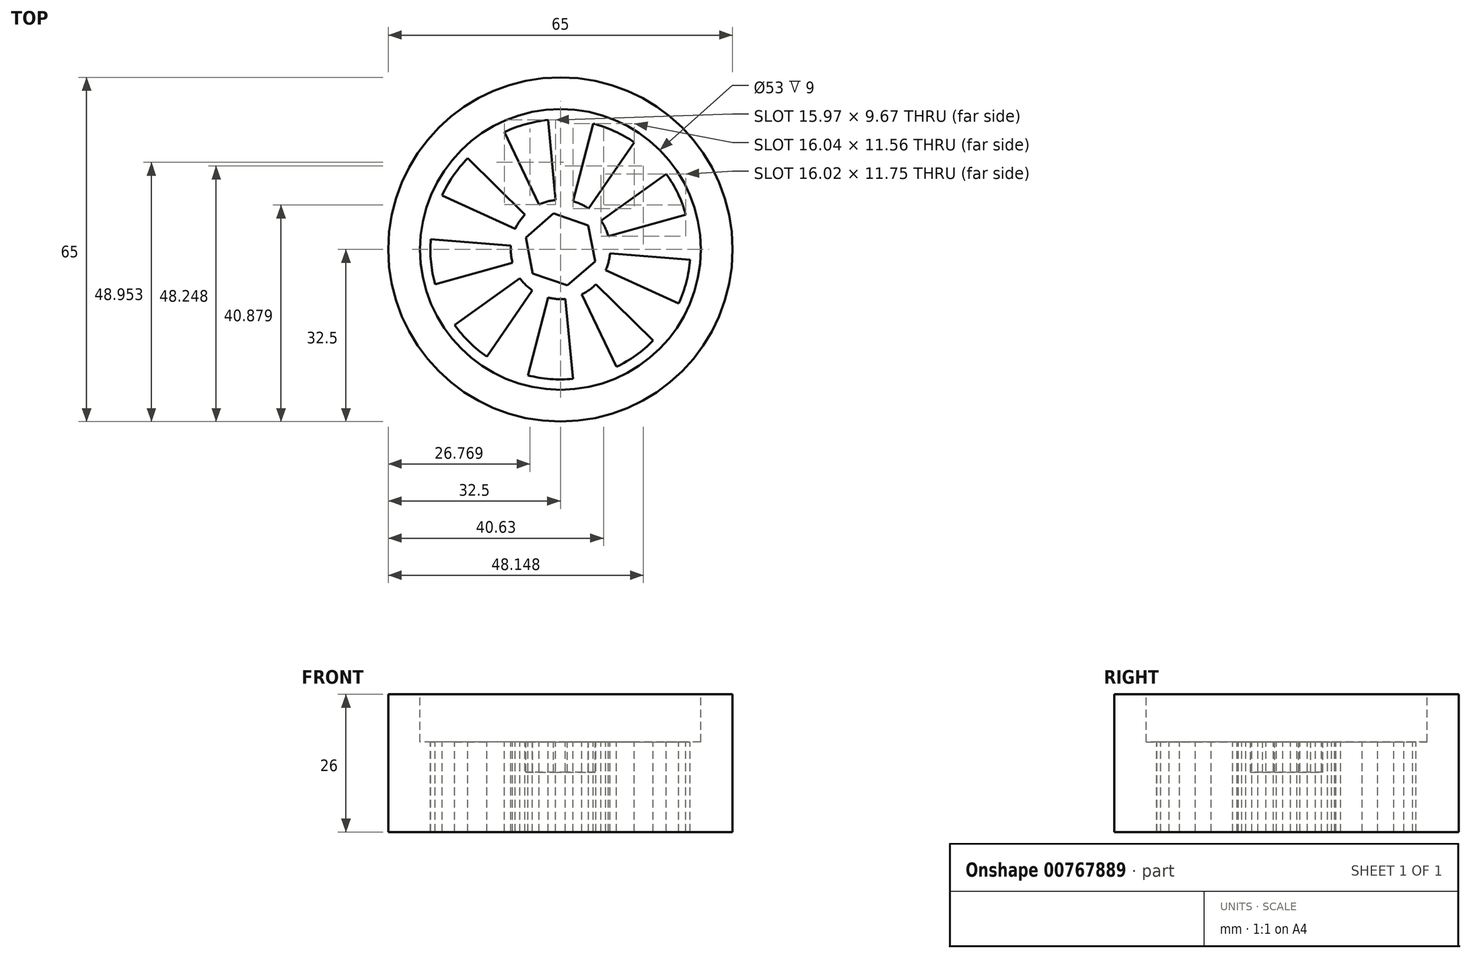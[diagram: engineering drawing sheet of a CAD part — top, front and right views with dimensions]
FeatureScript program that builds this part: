
annotation { "Feature Type Name" : "Feature", "Feature Type Description" : "" }
export const myFeature = defineFeature(function(context is Context, id is Id, definition is map)
    precondition{}
    {
        {
            var Q0;
            Q0=qCreatedBy(makeId("Top.planeOp"),FACE);
            var sketch = newSketch(context, id + "F0", { "sketchPlane" : qUnion([Q0])});
            skCircle(sketch, "E0", {"center": v(0, 0) * mm, "radius": 32.5 * mm});
            skSolve(sketch);
        }
        {
            var Q0;
            Q0=makeQuery(id+"F0.imprint","IMPRINT",FACE,{"disambiguationData":[TD([[makeQuery(id+"F0.imprint","IMPRINT",EDGE,{"derivedFrom":sQuery(id+"F0.wireOp",EDGE,"E0")}),1.0]])]});
            extrude(context, id + "F1", {"entities" : qUnion([Q0]), "depth" : 26 * mm, "offsetDistance" : 25 * mm});
        }
        {
            var Q0;
            Q0=makeQuery(id+"F1.opExtrude","CAP_FACE",FACE,{"disambiguationData":[OSD([sQuery(id+"F0.wireOp",EDGE,"E0")])],"isStart":false});
            var sketch = newSketch(context, id + "F2", { "sketchPlane" : qUnion([Q0])});
            skCircle(sketch, "E1.cCircle", {"center": v(0, 0) * mm, "radius": 6.93 * mm, "construction": true});
            skLineSegment(sketch, "E1.0", {"start": v(-5.24, -4.53) * mm, "end": v(-6.54, 2.27) * mm});
            skLineSegment(sketch, "E1.1", {"start": v(-6.54, 2.27) * mm, "end": v(-1.3, 6.8) * mm});
            skLineSegment(sketch, "E1.2", {"start": v(-1.3, 6.8) * mm, "end": v(5.24, 4.53) * mm});
            skLineSegment(sketch, "E1.3", {"start": v(5.24, 4.53) * mm, "end": v(6.54, -2.27) * mm});
            skLineSegment(sketch, "E1.4", {"start": v(6.54, -2.27) * mm, "end": v(1.3, -6.8) * mm});
            skLineSegment(sketch, "E1.5", {"start": v(1.3, -6.8) * mm, "end": v(-5.24, -4.53) * mm});
            skSolve(sketch);
        }
        {
            var Q0;
            Q0=makeQuery(id+"F2.imprint","IMPRINT",FACE,{"disambiguationData":[TD([[makeQuery(id+"F2.imprint","IMPRINT",EDGE,{"derivedFrom":sQuery(id+"F2.wireOp",EDGE,"E1.0")}),-1.0]])]});
            extrude(context, id + "F3", {"entities" : qUnion([Q0]), "operationType" : NewBodyOperationType.REMOVE, "oppositeDirection" : true, "depth" : 14.7 * mm, "offsetDistance" : 25 * mm});
        }
        {
            var Q0;
            Q0=makeQuery(id+"F1.opExtrude","CAP_FACE",FACE,{"disambiguationData":[OSD([sQuery(id+"F0.wireOp",EDGE,"E0")])],"isStart":false});
            var sketch = newSketch(context, id + "F4", { "sketchPlane" : qUnion([Q0])});
            skCircle(sketch, "E2", {"center": v(0, 0) * mm, "radius": 26.5 * mm});
            skSolve(sketch);
        }
        {
            var Q0;
            Q0=makeQuery(id+"F4.imprint","IMPRINT",FACE,{"disambiguationData":[TD([[makeQuery(id+"F4.imprint","IMPRINT",EDGE,{"derivedFrom":sQuery(id+"F4.wireOp",EDGE,"E2")}),1.0]])]});
            extrude(context, id + "F5", {"entities" : qUnion([Q0]), "operationType" : NewBodyOperationType.REMOVE, "oppositeDirection" : true, "depth" : 9 * mm, "offsetDistance" : 25 * mm});
        }
        {
            var Q0;
            Q0=makeQuery(id+"F5.boolean.opBoolean","COPY",FACE,{"derivedFrom":makeQuery(id+"F5.opExtrude","CAP_FACE",FACE,{"disambiguationData":[OSD([sQuery(id+"F2.wireOp",EDGE,"E1.0"),sQuery(id+"F2.wireOp",EDGE,"E1.1"),sQuery(id+"F2.wireOp",EDGE,"E1.2"),sQuery(id+"F2.wireOp",EDGE,"E1.3"),sQuery(id+"F2.wireOp",EDGE,"E1.4"),sQuery(id+"F2.wireOp",EDGE,"E1.5"),sQuery(id+"F4.wireOp",EDGE,"E2")])],"isStart":false})});
            var sketch = newSketch(context, id + "F6", { "sketchPlane" : qUnion([Q0])});
            skArc(sketch, "E3", {"start": v(-2.35, 24.44) * mm, "mid": v(-6.56, 23.66) * mm, "end": v(-10.56, 22.16) * mm});
            skLineSegment(sketch, "E4", {"start": v(-4.04, 8.47) * mm, "end": v(-10.56, 22.16) * mm});
            skLineSegment(sketch, "E5", {"start": v(-0.9, 9.34) * mm, "end": v(-2.35, 24.44) * mm});
            skArc(sketch, "E6", {"start": v(-0.9, 9.34) * mm, "mid": v(-2.5, 9.04) * mm, "end": v(-4.04, 8.47) * mm});
            skLineSegment(sketch, "E7.1.0", {"start": v(-8.53, 3.9) * mm, "end": v(-22.34, 10.19) * mm});
            skLineSegment(sketch, "E7.1.1", {"start": v(-6.69, 6.58) * mm, "end": v(-17.5, 17.21) * mm});
            skArc(sketch, "E7.1.2", {"start": v(-17.5, 17.21) * mm, "mid": v(-20.23, 13.91) * mm, "end": v(-22.34, 10.19) * mm});
            skArc(sketch, "E7.1.3", {"start": v(-6.69, 6.58) * mm, "mid": v(-7.73, 5.31) * mm, "end": v(-8.53, 3.9) * mm});
            skLineSegment(sketch, "E7.2.0", {"start": v(-9.04, -2.5) * mm, "end": v(-23.66, -6.56) * mm});
            skLineSegment(sketch, "E7.2.1", {"start": v(-9.35, 0.74) * mm, "end": v(-24.47, 1.93) * mm});
            skArc(sketch, "E7.2.2", {"start": v(-24.47, 1.93) * mm, "mid": v(-24.44, -2.35) * mm, "end": v(-23.66, -6.56) * mm});
            skArc(sketch, "E7.2.3", {"start": v(-9.35, 0.74) * mm, "mid": v(-9.34, -0.9) * mm, "end": v(-9.04, -2.5) * mm});
            skLineSegment(sketch, "E7.3.0", {"start": v(-5.31, -7.73) * mm, "end": v(-13.91, -20.23) * mm});
            skLineSegment(sketch, "E7.3.1", {"start": v(-7.64, -5.45) * mm, "end": v(-20, -14.25) * mm});
            skArc(sketch, "E7.3.2", {"start": v(-20, -14.25) * mm, "mid": v(-17.21, -17.5) * mm, "end": v(-13.91, -20.23) * mm});
            skArc(sketch, "E7.3.3", {"start": v(-7.64, -5.45) * mm, "mid": v(-6.58, -6.69) * mm, "end": v(-5.31, -7.73) * mm});
            skLineSegment(sketch, "E7.4.0", {"start": v(0.9, -9.34) * mm, "end": v(2.35, -24.44) * mm});
            skLineSegment(sketch, "E7.4.1", {"start": v(-2.35, -9.08) * mm, "end": v(-6.15, -23.77) * mm});
            skArc(sketch, "E7.4.2", {"start": v(-6.15, -23.77) * mm, "mid": v(-1.93, -24.47) * mm, "end": v(2.35, -24.44) * mm});
            skArc(sketch, "E7.4.3", {"start": v(-2.35, -9.08) * mm, "mid": v(-0.74, -9.35) * mm, "end": v(0.9, -9.34) * mm});
            skLineSegment(sketch, "E7.5.0", {"start": v(6.69, -6.58) * mm, "end": v(17.5, -17.21) * mm});
            skLineSegment(sketch, "E7.5.1", {"start": v(4.04, -8.47) * mm, "end": v(10.56, -22.16) * mm});
            skArc(sketch, "E7.5.2", {"start": v(10.56, -22.16) * mm, "mid": v(14.25, -20) * mm, "end": v(17.5, -17.21) * mm});
            skArc(sketch, "E7.5.3", {"start": v(4.04, -8.47) * mm, "mid": v(5.45, -7.64) * mm, "end": v(6.69, -6.58) * mm});
            skLineSegment(sketch, "E7.6.0", {"start": v(9.35, -0.74) * mm, "end": v(24.47, -1.93) * mm});
            skLineSegment(sketch, "E7.6.1", {"start": v(8.53, -3.9) * mm, "end": v(22.34, -10.19) * mm});
            skArc(sketch, "E7.6.2", {"start": v(22.34, -10.19) * mm, "mid": v(23.77, -6.15) * mm, "end": v(24.47, -1.93) * mm});
            skArc(sketch, "E7.6.3", {"start": v(8.53, -3.9) * mm, "mid": v(9.08, -2.35) * mm, "end": v(9.35, -0.74) * mm});
            skLineSegment(sketch, "E7.7.0", {"start": v(7.64, 5.45) * mm, "end": v(20, 14.25) * mm});
            skLineSegment(sketch, "E7.7.1", {"start": v(9.04, 2.5) * mm, "end": v(23.66, 6.56) * mm});
            skArc(sketch, "E7.7.2", {"start": v(23.66, 6.56) * mm, "mid": v(22.16, 10.56) * mm, "end": v(20, 14.25) * mm});
            skArc(sketch, "E7.7.3", {"start": v(9.04, 2.5) * mm, "mid": v(8.47, 4.04) * mm, "end": v(7.64, 5.45) * mm});
            skLineSegment(sketch, "E7.8.0", {"start": v(2.35, 9.08) * mm, "end": v(6.15, 23.77) * mm});
            skLineSegment(sketch, "E7.8.1", {"start": v(5.31, 7.73) * mm, "end": v(13.91, 20.23) * mm});
            skArc(sketch, "E7.8.2", {"start": v(13.91, 20.23) * mm, "mid": v(10.19, 22.34) * mm, "end": v(6.15, 23.77) * mm});
            skArc(sketch, "E7.8.3", {"start": v(5.31, 7.73) * mm, "mid": v(3.9, 8.53) * mm, "end": v(2.35, 9.08) * mm});
            skSolve(sketch);
        }
        {
            var Q0;
            Q0=makeQuery(id+"F6.imprint","IMPRINT",FACE,{"disambiguationData":[TD([[makeQuery(id+"F6.imprint","IMPRINT",EDGE,{"derivedFrom":sQuery(id+"F6.wireOp",EDGE,"E7.1.0")}),-1.0]])]});
            var Q1;
            Q1=makeQuery(id+"F6.imprint","IMPRINT",FACE,{"disambiguationData":[TD([[makeQuery(id+"F6.imprint","IMPRINT",EDGE,{"derivedFrom":sQuery(id+"F6.wireOp",EDGE,"E7.2.0")}),-1.0]])]});
            var Q2;
            Q2=makeQuery(id+"F6.imprint","IMPRINT",FACE,{"disambiguationData":[TD([[makeQuery(id+"F6.imprint","IMPRINT",EDGE,{"derivedFrom":sQuery(id+"F6.wireOp",EDGE,"E7.3.0")}),-1.0]])]});
            var Q3;
            Q3=makeQuery(id+"F6.imprint","IMPRINT",FACE,{"disambiguationData":[TD([[makeQuery(id+"F6.imprint","IMPRINT",EDGE,{"derivedFrom":sQuery(id+"F6.wireOp",EDGE,"E7.4.0")}),-1.0]])]});
            var Q4;
            Q4=makeQuery(id+"F6.imprint","IMPRINT",FACE,{"disambiguationData":[TD([[makeQuery(id+"F6.imprint","IMPRINT",EDGE,{"derivedFrom":sQuery(id+"F6.wireOp",EDGE,"E7.5.0")}),-1.0]])]});
            var Q5;
            Q5=makeQuery(id+"F6.imprint","IMPRINT",FACE,{"disambiguationData":[TD([[makeQuery(id+"F6.imprint","IMPRINT",EDGE,{"derivedFrom":sQuery(id+"F6.wireOp",EDGE,"E7.6.0")}),-1.0]])]});
            var Q6;
            Q6=makeQuery(id+"F6.imprint","IMPRINT",FACE,{"disambiguationData":[TD([[makeQuery(id+"F6.imprint","IMPRINT",EDGE,{"derivedFrom":sQuery(id+"F6.wireOp",EDGE,"E7.7.0")}),-1.0]])]});
            var Q7;
            Q7=makeQuery(id+"F6.imprint","IMPRINT",FACE,{"disambiguationData":[TD([[makeQuery(id+"F6.imprint","IMPRINT",EDGE,{"derivedFrom":sQuery(id+"F6.wireOp",EDGE,"E7.8.0")}),-1.0]])]});
            var Q8;
            Q8=makeQuery(id+"F6.imprint","IMPRINT",FACE,{"disambiguationData":[TD([[makeQuery(id+"F6.imprint","IMPRINT",EDGE,{"derivedFrom":sQuery(id+"F6.wireOp",EDGE,"E3")}),1.0]])]});
            extrude(context, id + "F7", {"entities" : qUnion([Q0, Q1, Q2, Q3, Q4, Q5, Q6, Q7, Q8]), "operationType" : NewBodyOperationType.REMOVE, "oppositeDirection" : true, "depth" : 25 * mm, "offsetDistance" : 25 * mm});
        }
    });
